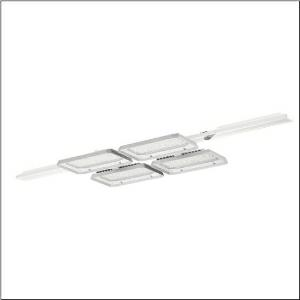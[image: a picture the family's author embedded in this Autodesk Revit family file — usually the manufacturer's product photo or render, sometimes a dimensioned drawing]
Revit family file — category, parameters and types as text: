
# Revit family: highbay_21_51hla1d24mlb
name_source: partatom
category: Lighting Fixtures
units: mm (PartAtom-declared; Revit-internal decimal feet)

## family parameters
Cut with Voids When Loaded = No
Host = Face
Light Source = No
Part Type = Normal
Room Calculation Point = No
Round Connector Dimension = Use Diameter
Shared = No

## types (1)
- --- (1 x LED, 26940 lm, 171.1 W, 4000K)
    Apparent Load = 171 VA
    CIE Flux Codes = 88 95 99 100 99
    Color Rendering = 80
    Color Temperature = 4000K
    Default Elevation = 1800 mm
    Description = Highbay 21, LED high bay luminaire, end cap, primary light control with lens, of PMMA, light emission: direct distribution, primary light characteristic: symmetric, installation type: recessed, for 2x 2 x LED rated luminous flux: 26.940 lm, light colour: 840, colour temperature: 4000K, control gear: ECG DALI, with system connector, mains connection: 230..240V, AC, 50/60Hz, rated input power: 171W, LED unit, of diecast aluminium, unplated, bead blasted, silver, length: 1.500 mm, width: 500 mm, height: 65mm, housing, of diecast aluminium, uncoated, bead blasted, silver, fixing on rail side, of aluminium, anodised, metallic grey, end cap, of PC, grey, protection rating (complete): IP64, insulation class (complete): insulation class I (protective earthing), certification: CE, protection symbol: D, impact resistance: IK08 with glass or PC cover, permissible ambient temperature for indoor applications: -35..+40°C, corresponds to IFS (International Featured Standards) requirements for safety and quality in the food industry, reducing of maximum allowable ambient temperature of 5°C with ceiling mounting, packaging unit: 1 piece
    Height = 105 mm
    Lamp = 1 x LED
    Lamp Light Flux = 26940 lm
    Lamp Power = 171.1 W
    Lamp count = 1
    Length = 1500 mm
    Luminous efficacy = 157 lm/W
    Manufacturer = Siteco
    ModVariant = No
    Model = 51HLA1D24MLB
    Mounting Place = Ceiling
    Mounting Type = Pendant
    Number of Poles = 1
    OnlyDefault = Yes
    Power Factor = 1
    Product Name = Highbay 21
    Product group = LED high bay luminaire
    ProductGroupID = 903
    Protection Class = Protection class I
    Protection Degree = IP 64
    RLX_Detail_Level = 1
    RlxData = <blob elided: 40749 chars, md5=e03027e7>
    Socket = socket
    Standby Power = 0 W
    System Light Flux = 26940 lm
    System Power = 171 W
    Type Comments = factory setting: luminous flux: 100 % | dim-lin: 254 | 490 mA
    Type Image = l_1004707.jpg
    URL = http://relux.com
    VarID = @adj_135813
    Voltage = 0 V
    Weight = 0.00 kg
    Width = 500 mm

## geometry (parser evidence)
native form markers: Blend x4, Sweep x11
no freeform markers — native parametric forms only
